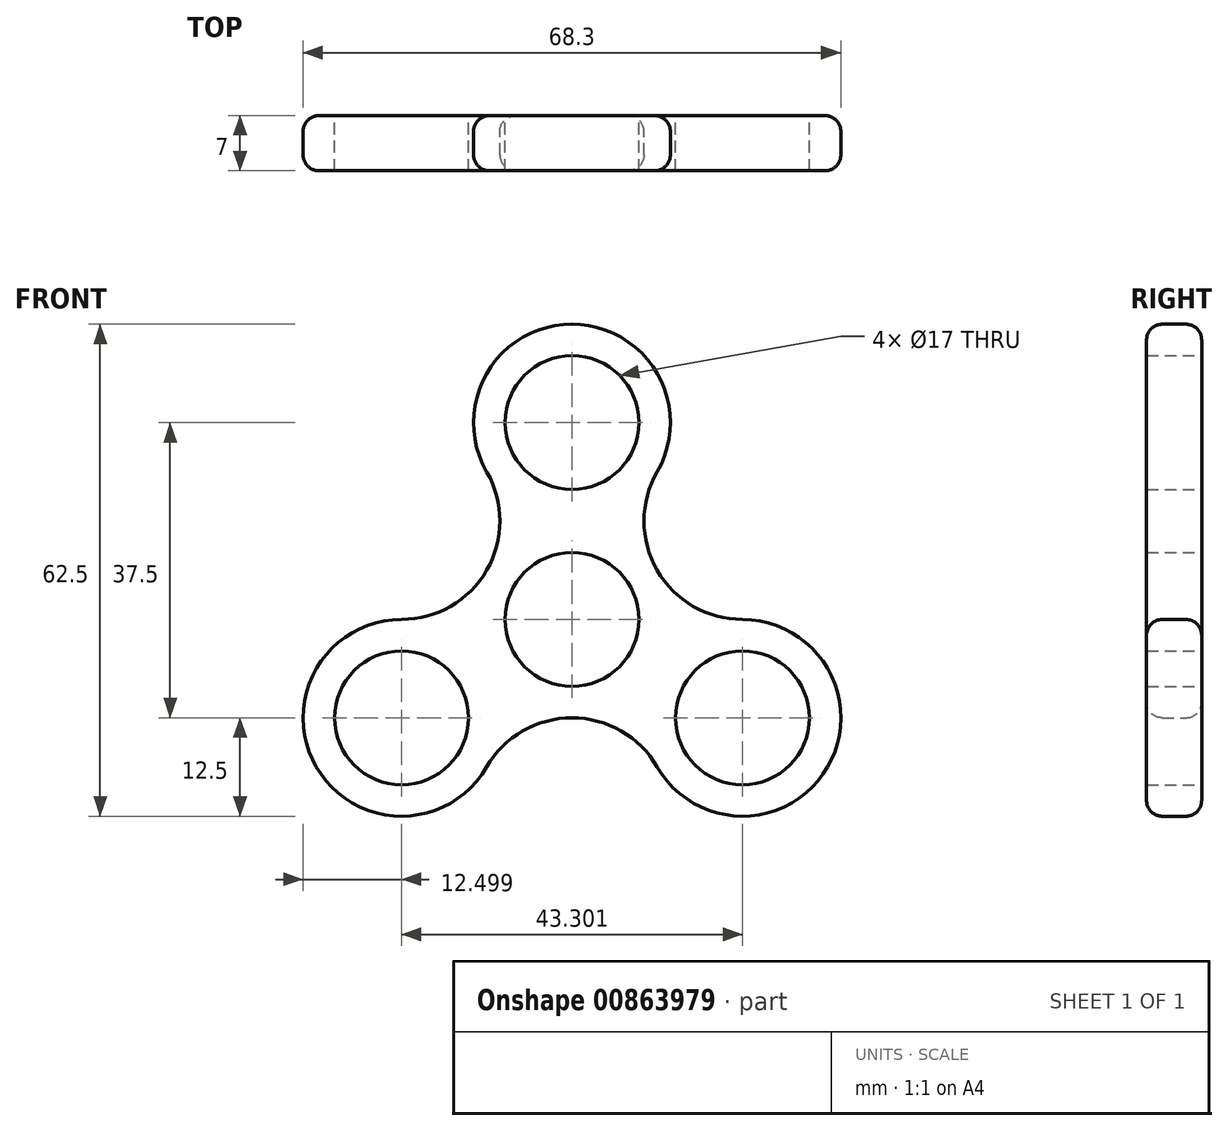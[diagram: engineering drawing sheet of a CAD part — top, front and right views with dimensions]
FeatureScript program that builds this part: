
annotation { "Feature Type Name" : "Feature", "Feature Type Description" : "" }
export const myFeature = defineFeature(function(context is Context, id is Id, definition is map)
    precondition{}
    {
        {
            var Q0;
            Q0=qCreatedBy(makeId("Front.planeOp"),FACE);
            var sketch = newSketch(context, id + "F0", { "sketchPlane" : qUnion([Q0])});
            skCircle(sketch, "E0", {"center": v(0, 0) * mm, "radius": 8.5 * mm});
            skCircle(sketch, "E1", {"center": v(0, 25) * mm, "radius": 8.5 * mm});
            skCircle(sketch, "E2.1.0", {"center": v(-21.65, -12.5) * mm, "radius": 8.5 * mm});
            skCircle(sketch, "E2.2.0", {"center": v(21.65, -12.5) * mm, "radius": 8.5 * mm});
            skArc(sketch, "E3", {"start": v(10.83, 18.75) * mm, "mid": v(0, 37.5) * mm, "end": v(-10.83, 18.75) * mm});
            skArc(sketch, "E4.1.0", {"start": v(-21.65, 0) * mm, "mid": v(-10.83, 6.25) * mm, "end": v(-10.83, 18.75) * mm});
            skArc(sketch, "E4.2.0", {"start": v(-21.65, 0) * mm, "mid": v(-32.48, -18.75) * mm, "end": v(-10.83, -18.75) * mm});
            skArc(sketch, "E4.3.0", {"start": v(10.83, -18.75) * mm, "mid": v(0, -12.5) * mm, "end": v(-10.83, -18.75) * mm});
            skArc(sketch, "E4.4.0", {"start": v(10.83, -18.75) * mm, "mid": v(32.48, -18.75) * mm, "end": v(21.65, 0) * mm});
            skArc(sketch, "E4.5.0", {"start": v(10.83, 18.75) * mm, "mid": v(10.83, 6.25) * mm, "end": v(21.65, 0) * mm});
            skSolve(sketch);
        }
        {
            var Q0;
            Q0=makeQuery(id+"F0.imprint","IMPRINT",FACE,{"disambiguationData":[TD([[makeQuery(id+"F0.imprint","IMPRINT",EDGE,{"derivedFrom":sQuery(id+"F0.wireOp",EDGE,"E0")}),-1.0]])]});
            extrude(context, id + "F1", {"entities" : qUnion([Q0]), "depth" : 7 * mm, "offsetDistance" : 25 * mm});
        }
        {
            var Q0;
            Q0=makeQuery(id+"F1.opExtrude","CAP_EDGE",EDGE,{"disambiguationData":[OSD([sQuery(id+"F0.wireOp",EDGE,"E4.1.0")])],"isStart":true});
            var Q1;
            Q1=makeQuery(id+"F1.opExtrude","CAP_EDGE",EDGE,{"disambiguationData":[OSD([sQuery(id+"F0.wireOp",EDGE,"E4.1.0")])],"isStart":false});
            fillet(context, id + "F2", {"entities" : qUnion([Q0, Q1]), "radius" : 2 * mm, "tangentPropagation" : true, "allowEdgeOverflow" : false});
        }
    });
